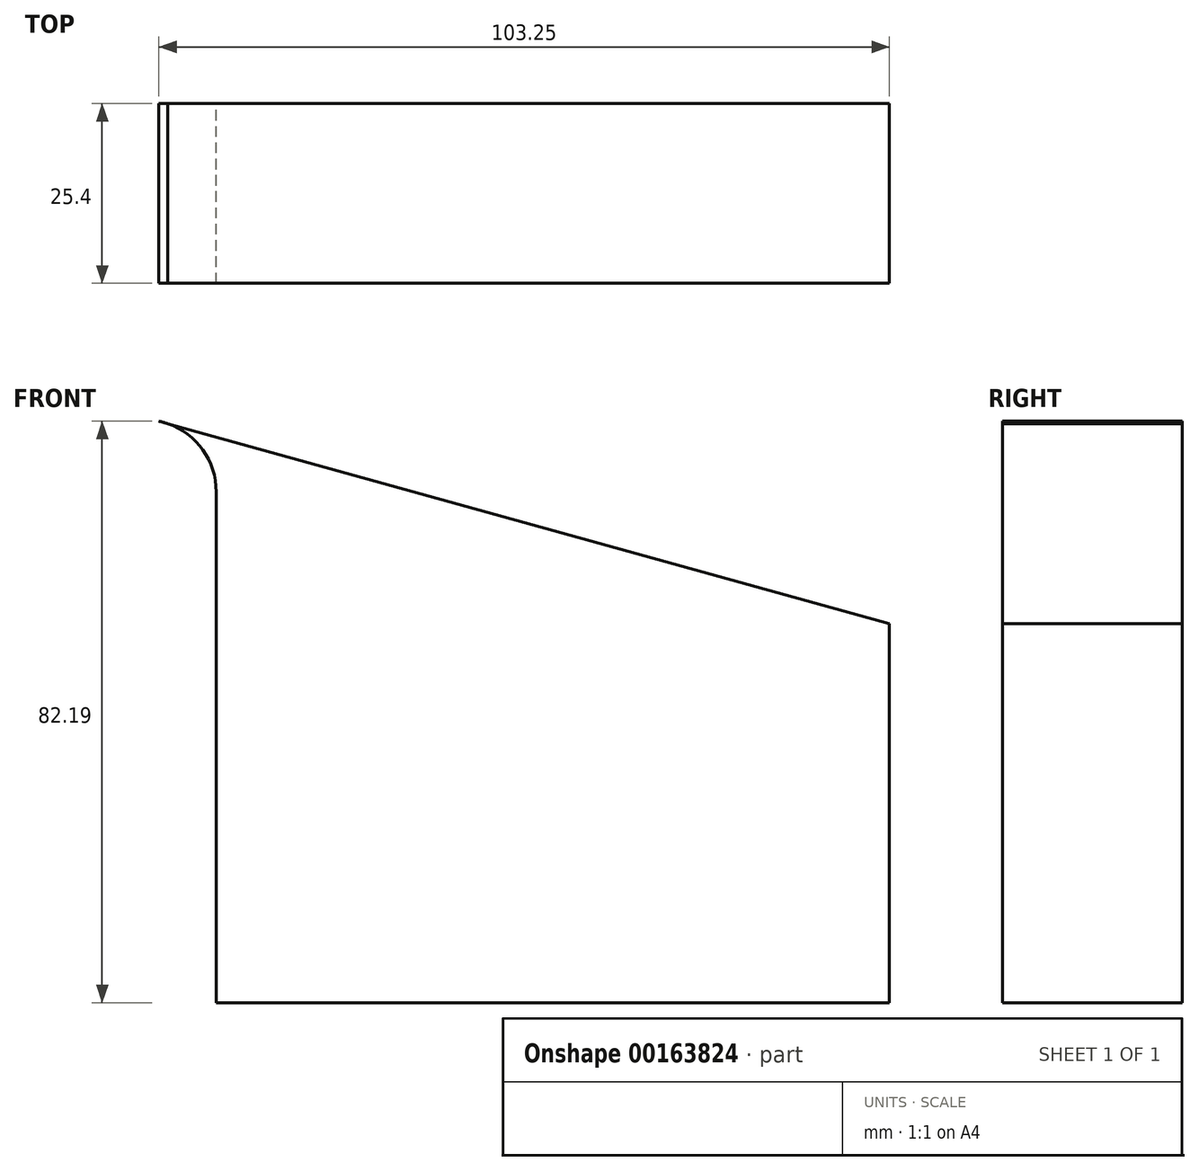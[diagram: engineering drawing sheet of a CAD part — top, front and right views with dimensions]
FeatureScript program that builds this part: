
annotation { "Feature Type Name" : "Feature", "Feature Type Description" : "" }
export const myFeature = defineFeature(function(context is Context, id is Id, definition is map)
    precondition{}
    {
        {
            var Q0;
            Q0=qCreatedBy(makeId("Front.planeOp"),FACE);
            var sketch = newSketch(context, id + "F0", { "sketchPlane" : qUnion([Q0])});
            skLineSegment(sketch, "E0.bottom", {"start": v(-47.57, 26.8) * mm, "end": v(47.57, 26.8) * mm});
            skLineSegment(sketch, "E0.top", {"start": v(-47.57, -26.8) * mm, "end": v(47.57, -26.8) * mm});
            skLineSegment(sketch, "E0.left", {"start": v(-47.57, 26.8) * mm, "end": v(-47.57, -26.8) * mm});
            skLineSegment(sketch, "E0.right", {"start": v(47.57, 26.8) * mm, "end": v(47.57, -26.8) * mm});
            skPoint(sketch, "E0.middle", {"position": v(0, 0) * mm});
            skLineSegment(sketch, "E1", {"start": v(-47.57, 26.8) * mm, "end": v(-47.57, 45.42) * mm});
            skArc(sketch, "E2", {"start": v(-47.57, 45.42) * mm, "mid": v(-50.8, 52.87) * mm, "end": v(-58.46, 55.6) * mm});
            skLineSegment(sketch, "E3", {"start": v(47.57, 26.8) * mm, "end": v(-61.05, 56.89) * mm});
            skSolve(sketch);
        }
        {
            var Q0;
            Q0 = qSketchRegion(id + "F0", true);
            extrude(context, id + "F1", {"entities" : qUnion([Q0]), "depth" : 25.4 * mm});
        }
    });
